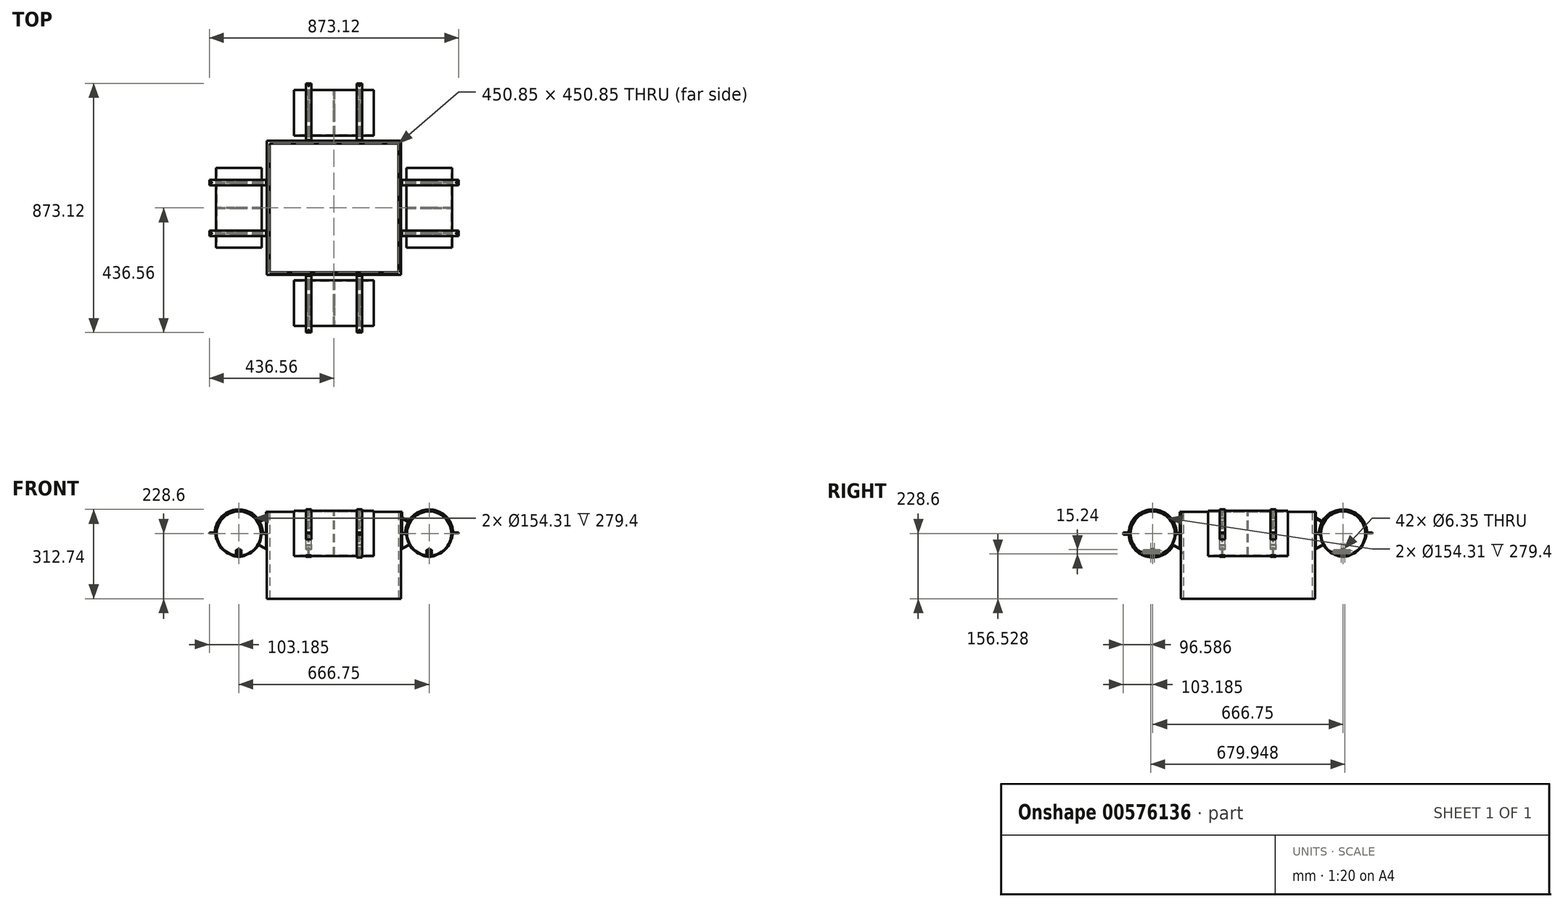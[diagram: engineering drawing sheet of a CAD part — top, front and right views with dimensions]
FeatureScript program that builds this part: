
annotation { "Feature Type Name" : "Feature", "Feature Type Description" : "" }
export const myFeature = defineFeature(function(context is Context, id is Id, definition is map)
    precondition{}
    {
        {
            var Q0;
            Q0=qCreatedBy(makeId("Front.planeOp"),FACE);
            var sketch = newSketch(context, id + "F0", { "sketchPlane" : qUnion([Q0])});
            skLineSegment(sketch, "E0", {"start": v(0, 0) * mm, "end": v(238.13, 0) * mm});
            skLineSegment(sketch, "E1", {"start": v(238.13, 0) * mm, "end": v(238.13, 228.6) * mm});
            skLineSegment(sketch, "E2", {"start": v(238.13, 228.6) * mm, "end": v(333.38, 228.6) * mm});
            skCircle(sketch, "E3", {"center": v(333.38, 228.6) * mm, "radius": 79.7 * mm});
            skCircle(sketch, "E4", {"center": v(333.38, 228.6) * mm, "radius": 77.15 * mm});
            skSolve(sketch);
        }
        {
            var Q0;
            Q0=qSketchRegion(id+"F0",true);
            extrude(context, id + "F1", {"entities" : qUnion([Q0]), "endBound" : BoundingType.SYMMETRIC, "depth" : 279.4 * mm, "offsetDistance" : 25.4 * mm});
        }
        {
            var Q0;
            Q0=qCreatedBy(makeId("Front.planeOp"),FACE);
            var sketch = newSketch(context, id + "F2", { "sketchPlane" : qUnion([Q0])});
            skLineSegment(sketch, "E5", {"start": v(0, 0) * mm, "end": v(0, 120.85) * mm});
            skSolve(sketch);
        }
        {
            var Q0;
            Q0=makeQuery(id+"F1.opExtrude","SWEPT_BODY",BODY,{"disambiguationData":[OSD([sQuery(id+"F0.wireOp",EDGE,"E3"),sQuery(id+"F0.wireOp",EDGE,"E4")])]});
            var Q1;
            Q1=sQuery(id+"F2.wireOp",EDGE,"E5");
            circularPattern(context, id + "F3", {"entities" : qUnion([Q0]), "axis" : qUnion([Q1]), "angle" : 360 * degree, "instanceCount" : 4, "equalSpace" : true});
        }
        {
            var Q0;
            Q0=qCreatedBy(makeId("Top.planeOp"),FACE);
            var sketch = newSketch(context, id + "F4", { "sketchPlane" : qUnion([Q0])});
            skLineSegment(sketch, "E6.bottom", {"start": v(234.95, -234.95) * mm, "end": v(-234.95, -234.95) * mm});
            skLineSegment(sketch, "E6.top", {"start": v(234.95, 234.95) * mm, "end": v(-234.95, 234.95) * mm});
            skLineSegment(sketch, "E6.left", {"start": v(234.95, -234.95) * mm, "end": v(234.95, 234.95) * mm});
            skLineSegment(sketch, "E6.right", {"start": v(-234.95, -234.95) * mm, "end": v(-234.95, 234.95) * mm});
            skPoint(sketch, "E6.middle", {"position": v(0, 0) * mm});
            skLineSegment(sketch, "E7.0", {"start": v(225.42, -225.42) * mm, "end": v(-225.43, -225.43) * mm});
            skLineSegment(sketch, "E7.1", {"start": v(225.42, -225.42) * mm, "end": v(225.43, 225.43) * mm});
            skLineSegment(sketch, "E7.2", {"start": v(225.43, 225.43) * mm, "end": v(-225.43, 225.43) * mm});
            skLineSegment(sketch, "E7.3", {"start": v(-225.43, -225.43) * mm, "end": v(-225.43, 225.43) * mm});
            skSolve(sketch);
        }
        {
            var Q0;
            Q0=qSketchRegion(id+"F4",true);
            extrude(context, id + "F5", {"entities" : qUnion([Q0]), "depth" : 304.8 * mm, "offsetDistance" : 25.4 * mm});
        }
        {
            var Q0;
            Q0=qCreatedBy(makeId("Right.planeOp"),FACE);
            cPlane(context, id + "F6", {"entities" : qUnion([Q0]), "cplaneType" : CPlaneType.OFFSET, "offset" : 88.9 * mm, "width" : 152.4 * mm, "height" : 152.4 * mm});
        }
        {
            var Q0;
            Q0=qCreatedBy(makeId("Right.planeOp"),FACE);
            cPlane(context, id + "F7", {"entities" : qUnion([Q0]), "cplaneType" : CPlaneType.OFFSET, "offset" : 88.9 * mm, "oppositeDirection" : true, "width" : 152.4 * mm, "height" : 152.4 * mm});
        }
        {
            var Q0;
            Q0=qCreatedBy(makeId("Right.planeOp"),FACE);
            var sketch = newSketch(context, id + "F8", { "sketchPlane" : qUnion([Q0])});
            skCircle(sketch, "E8", {"center": v(-333.38, 228.6) * mm, "radius": 77.15 * mm});
            skLineSegment(sketch, "E9", {"start": v(-333.38, 228.6) * mm, "end": v(-333.38, 151.45) * mm});
            skLineSegment(sketch, "E10", {"start": v(-333.38, 151.45) * mm, "end": v(-333.38, 156.53) * mm});
            skCircle(sketch, "E11", {"center": v(-333.38, 156.53) * mm, "radius": 3.18 * mm});
            skLineSegment(sketch, "E12", {"start": v(-333.38, 156.53) * mm, "end": v(-333.38, 164.15) * mm});
            skCircle(sketch, "E13", {"center": v(-333.38, 164.15) * mm, "radius": 3.18 * mm});
            skCircle(sketch, "E14.1.0", {"center": v(-326.78, 160.34) * mm, "radius": 3.18 * mm});
            skCircle(sketch, "E14.2.0", {"center": v(-326.78, 167.96) * mm, "radius": 3.18 * mm});
            skCircle(sketch, "E14.3.0", {"center": v(-333.38, 171.77) * mm, "radius": 3.18 * mm});
            skCircle(sketch, "E14.4.0", {"center": v(-339.97, 167.96) * mm, "radius": 3.18 * mm});
            skCircle(sketch, "E14.5.0", {"center": v(-339.97, 160.34) * mm, "radius": 3.18 * mm});
            skSolve(sketch);
        }
        {
            var Q0;
            Q0=qSketchRegion(id+"F8",true);
            extrude(context, id + "F9", {"entities" : qUnion([Q0]), "endBound" : BoundingType.SYMMETRIC, "depth" : 3.17 * mm, "offsetDistance" : 25.4 * mm});
        }
        {
            var Q0;
            Q0=qCreatedBy(id+"F6.planeOp",FACE);
            cPlane(context, id + "F10", {"entities" : qUnion([Q0]), "cplaneType" : CPlaneType.OFFSET, "offset" : 44.45 * mm, "oppositeDirection" : true, "width" : 152.4 * mm, "height" : 152.4 * mm});
        }
        {
            var Q0;
            Q0=qCreatedBy(id+"F7.planeOp",FACE);
            cPlane(context, id + "F11", {"entities" : qUnion([Q0]), "cplaneType" : CPlaneType.OFFSET, "offset" : 44.45 * mm, "width" : 152.4 * mm, "height" : 152.4 * mm});
        }
        {
            var Q0;
            Q0=makeQuery(id+"F9.opExtrude","SWEPT_BODY",BODY,{"disambiguationData":[OSD([sQuery(id+"F8.wireOp",EDGE,"E8"),sQuery(id+"F8.wireOp",EDGE,"E11"),sQuery(id+"F8.wireOp",EDGE,"E13"),sQuery(id+"F8.wireOp",EDGE,"E14.1.0"),sQuery(id+"F8.wireOp",EDGE,"E14.2.0"),sQuery(id+"F8.wireOp",EDGE,"E14.3.0"),sQuery(id+"F8.wireOp",EDGE,"E14.4.0"),sQuery(id+"F8.wireOp",EDGE,"E14.5.0")])]});
            var Q1;
            Q1=qCreatedBy(id+"F11.planeOp",FACE);
            mirror(context, id + "F12", {"entities" : qUnion([Q0]), "mirrorPlane" : qUnion([Q1])});
        }
        {
            var Q0;
            Q0=makeQuery(id+"F9.opExtrude","SWEPT_BODY",BODY,{"disambiguationData":[OSD([sQuery(id+"F8.wireOp",EDGE,"E8"),sQuery(id+"F8.wireOp",EDGE,"E11"),sQuery(id+"F8.wireOp",EDGE,"E13"),sQuery(id+"F8.wireOp",EDGE,"E14.1.0"),sQuery(id+"F8.wireOp",EDGE,"E14.2.0"),sQuery(id+"F8.wireOp",EDGE,"E14.3.0"),sQuery(id+"F8.wireOp",EDGE,"E14.4.0"),sQuery(id+"F8.wireOp",EDGE,"E14.5.0")])]});
            var Q1;
            Q1=qCreatedBy(id+"F10.planeOp",FACE);
            mirror(context, id + "F13", {"entities" : qUnion([Q0]), "mirrorPlane" : qUnion([Q1])});
        }
        {
            var Q0;
            Q0=makeQuery(id+"F13.opPattern","COPY",BODY,{"derivedFrom":makeQuery(id+"F9.opExtrude","SWEPT_BODY",BODY,{"disambiguationData":[OSD([sQuery(id+"F8.wireOp",EDGE,"E8"),sQuery(id+"F8.wireOp",EDGE,"E11"),sQuery(id+"F8.wireOp",EDGE,"E13"),sQuery(id+"F8.wireOp",EDGE,"E14.1.0"),sQuery(id+"F8.wireOp",EDGE,"E14.2.0"),sQuery(id+"F8.wireOp",EDGE,"E14.3.0"),sQuery(id+"F8.wireOp",EDGE,"E14.4.0"),sQuery(id+"F8.wireOp",EDGE,"E14.5.0")])]}),"instanceName":"1"});
            var Q1;
            Q1=makeQuery(id+"F12.opPattern","COPY",BODY,{"derivedFrom":makeQuery(id+"F9.opExtrude","SWEPT_BODY",BODY,{"disambiguationData":[OSD([sQuery(id+"F8.wireOp",EDGE,"E8"),sQuery(id+"F8.wireOp",EDGE,"E11"),sQuery(id+"F8.wireOp",EDGE,"E13"),sQuery(id+"F8.wireOp",EDGE,"E14.1.0"),sQuery(id+"F8.wireOp",EDGE,"E14.2.0"),sQuery(id+"F8.wireOp",EDGE,"E14.3.0"),sQuery(id+"F8.wireOp",EDGE,"E14.4.0"),sQuery(id+"F8.wireOp",EDGE,"E14.5.0")])]}),"instanceName":"1"});
            var Q2;
            Q2=makeQuery(id+"F9.opExtrude","SWEPT_BODY",BODY,{"disambiguationData":[OSD([sQuery(id+"F8.wireOp",EDGE,"E8"),sQuery(id+"F8.wireOp",EDGE,"E11"),sQuery(id+"F8.wireOp",EDGE,"E13"),sQuery(id+"F8.wireOp",EDGE,"E14.1.0"),sQuery(id+"F8.wireOp",EDGE,"E14.2.0"),sQuery(id+"F8.wireOp",EDGE,"E14.3.0"),sQuery(id+"F8.wireOp",EDGE,"E14.4.0"),sQuery(id+"F8.wireOp",EDGE,"E14.5.0")])]});
            var Q3;
            Q3=sQuery(id+"F2.wireOp",EDGE,"E5");
            circularPattern(context, id + "F14", {"entities" : qUnion([Q0, Q1, Q2]), "axis" : qUnion([Q3]), "angle" : 360 * degree, "instanceCount" : 4, "equalSpace" : true});
        }
        {
            var Q0;
            Q0=qCreatedBy(id+"F6.planeOp",FACE);
            var sketch = newSketch(context, id + "F15", { "sketchPlane" : qUnion([Q0])});
            skCircle(sketch, "E15", {"center": v(-333.38, 228.6) * mm, "radius": 81.28 * mm});
            skCircle(sketch, "E16", {"center": v(-333.38, 228.6) * mm, "radius": 79.7 * mm});
            skLineSegment(sketch, "E17", {"start": v(-333.38, 228.6) * mm, "end": v(-333.38, 309.88) * mm});
            skLineSegment(sketch, "E18", {"start": v(-333.38, 228.6) * mm, "end": v(-312.34, 307.11) * mm});
            skLineSegment(sketch, "E19.MirrorCS", {"start": v(-333.38, 228.6) * mm, "end": v(-354.41, 307.11) * mm});
            skLineSegment(sketch, "E20.1.0", {"start": v(-333.38, 228.6) * mm, "end": v(-411.89, 249.64) * mm});
            skLineSegment(sketch, "E20.1.1", {"start": v(-333.38, 228.6) * mm, "end": v(-411.89, 207.56) * mm});
            skLineSegment(sketch, "E20.2.0", {"start": v(-333.38, 228.6) * mm, "end": v(-354.41, 150.09) * mm});
            skLineSegment(sketch, "E20.2.1", {"start": v(-333.38, 228.6) * mm, "end": v(-312.34, 150.09) * mm});
            skLineSegment(sketch, "E20.3.0", {"start": v(-333.38, 228.6) * mm, "end": v(-254.86, 207.56) * mm});
            skLineSegment(sketch, "E20.3.1", {"start": v(-333.38, 228.6) * mm, "end": v(-254.86, 249.64) * mm});
            skLineSegment(sketch, "E21", {"start": v(-414.66, 228.6) * mm, "end": v(-417.51, 228.6) * mm});
            skLineSegment(sketch, "E22", {"start": v(-417.51, 228.6) * mm, "end": v(-436.56, 228.6) * mm});
            skLineSegment(sketch, "E23", {"start": v(-436.56, 229.1) * mm, "end": v(-436.56, 232.28) * mm});
            skLineSegment(sketch, "E24", {"start": v(-436.56, 232.28) * mm, "end": v(-419.83, 232.28) * mm});
            skLineSegment(sketch, "E25", {"start": v(-436.56, 229.1) * mm, "end": v(-417.51, 229.1) * mm});
            skLineSegment(sketch, "E26", {"start": v(-417.51, 229.1) * mm, "end": v(-414.65, 229.1) * mm});
            skPoint(sketch, "E27.visualSharp", {"position": v(-417.43, 232.28) * mm});
            skArc(sketch, "E27.filletArc", {"start": v(-419.83, 232.28) * mm, "mid": v(-418.1, 232.96) * mm, "end": v(-417.3, 234.64) * mm});
            skLineSegment(sketch, "E28.MirrorCS", {"start": v(-436.56, 228.1) * mm, "end": v(-417.51, 228.1) * mm});
            skPoint(sketch, "E29.MirrorP", {"position": v(-417.43, 224.92) * mm});
            skArc(sketch, "E30.MirrorCS", {"start": v(-419.83, 224.92) * mm, "mid": v(-418.1, 224.24) * mm, "end": v(-417.3, 222.56) * mm});
            skLineSegment(sketch, "E31.MirrorCS", {"start": v(-436.56, 224.92) * mm, "end": v(-419.83, 224.92) * mm});
            skLineSegment(sketch, "E32.MirrorCS", {"start": v(-436.56, 228.1) * mm, "end": v(-436.56, 224.92) * mm});
            skArc(sketch, "E33.trimOffspring", {"start": v(-417.3, 222.56) * mm, "mid": v(-330.35, 144.52) * mm, "end": v(-249.24, 228.6) * mm});
            skPoint(sketch, "E34.MirrorCS.start.orphan", {"position": v(-436.56, 228.6) * mm});
            skLineSegment(sketch, "E35", {"start": v(-417.51, 228.1) * mm, "end": v(-414.65, 228.1) * mm});
            skLineSegment(sketch, "E36", {"start": v(-333.38, 228.6) * mm, "end": v(-249.24, 228.6) * mm});
            skLineSegment(sketch, "E37", {"start": v(-249.24, 228.6) * mm, "end": v(-234.95, 228.6) * mm});
            skLineSegment(sketch, "E38", {"start": v(-333.38, 228.6) * mm, "end": v(-260.5, 270.67) * mm});
            skLineSegment(sketch, "E39", {"start": v(-260.5, 270.67) * mm, "end": v(-234.95, 285.43) * mm});
            skLineSegment(sketch, "E40", {"start": v(-234.95, 285.43) * mm, "end": v(-234.95, 304.48) * mm});
            skLineSegment(sketch, "E41", {"start": v(-234.95, 304.48) * mm, "end": v(-238.12, 304.48) * mm});
            skLineSegment(sketch, "E42", {"start": v(-238.13, 304.48) * mm, "end": v(-238.13, 286.9) * mm});
            skLineSegment(sketch, "E43", {"start": v(-234.95, 228.6) * mm, "end": v(-234.95, 230.19) * mm});
            skLineSegment(sketch, "E44", {"start": v(-240.67, 230.19) * mm, "end": v(-246.8, 230.19) * mm});
            skLineSegment(sketch, "E45", {"start": v(-234.95, 304.48) * mm, "end": v(-234.95, 228.6) * mm});
            skArc(sketch, "E46.trimOffspring", {"start": v(-249.33, 232.6) * mm, "mid": v(-252.1, 250.38) * mm, "end": v(-258.59, 267.15) * mm});
            skLineSegment(sketch, "E47", {"start": v(-234.95, 285.43) * mm, "end": v(-235.74, 286.8) * mm});
            skLineSegment(sketch, "E48", {"start": v(-234.95, 285.43) * mm, "end": v(-234.16, 284.05) * mm});
            skLineSegment(sketch, "E49", {"start": v(-234.16, 284.05) * mm, "end": v(-234.95, 283.6) * mm});
            skLineSegment(sketch, "E50", {"start": v(-239.4, 284.7) * mm, "end": v(-259.19, 273.26) * mm});
            skArc(sketch, "E51.trimOffspring", {"start": v(-262.6, 274.1) * mm, "mid": v(-354.17, 310.13) * mm, "end": v(-417.3, 234.64) * mm});
            skLineSegment(sketch, "E52.trimOffspring", {"start": v(-238.13, 277.36) * mm, "end": v(-238.13, 232.73) * mm});
            skLineSegment(sketch, "E53.trimOffspring", {"start": v(-241.94, 279.56) * mm, "end": v(-257.6, 270.51) * mm});
            skPoint(sketch, "E54.visualSharp", {"position": v(-238.13, 285.43) * mm});
            skArc(sketch, "E54.filletArc", {"start": v(-239.4, 284.7) * mm, "mid": v(-238.47, 285.62) * mm, "end": v(-238.12, 286.9) * mm});
            skPoint(sketch, "E55.visualSharp", {"position": v(-261.32, 272.04) * mm});
            skArc(sketch, "E55.filletArc", {"start": v(-262.6, 274.1) * mm, "mid": v(-261.06, 273) * mm, "end": v(-259.19, 273.26) * mm});
            skPoint(sketch, "E56.visualSharp", {"position": v(-259.73, 269.29) * mm});
            skArc(sketch, "E56.filletArc", {"start": v(-257.6, 270.51) * mm, "mid": v(-258.77, 269.03) * mm, "end": v(-258.59, 267.15) * mm});
            skPoint(sketch, "E57.visualSharp", {"position": v(-238.13, 281.76) * mm});
            skArc(sketch, "E57.filletArc", {"start": v(-238.13, 277.36) * mm, "mid": v(-239.4, 279.56) * mm, "end": v(-241.94, 279.56) * mm});
            skPoint(sketch, "E58.visualSharp", {"position": v(-249.25, 230.19) * mm});
            skArc(sketch, "E58.filletArc", {"start": v(-249.33, 232.6) * mm, "mid": v(-248.55, 230.89) * mm, "end": v(-246.8, 230.19) * mm});
            skPoint(sketch, "E59.visualSharp", {"position": v(-238.13, 230.19) * mm});
            skArc(sketch, "E59.filletArc", {"start": v(-240.67, 230.19) * mm, "mid": v(-238.87, 230.93) * mm, "end": v(-238.13, 232.73) * mm});
            skLineSegment(sketch, "E60.MirrorCS", {"start": v(-234.95, 171.77) * mm, "end": v(-235.74, 170.4) * mm});
            skLineSegment(sketch, "E61.MirrorCS", {"start": v(-234.95, 171.77) * mm, "end": v(-234.16, 173.15) * mm});
            skLineSegment(sketch, "E62.MirrorCS", {"start": v(-234.16, 173.15) * mm, "end": v(-234.95, 173.6) * mm});
            skArc(sketch, "E63.MirrorCS", {"start": v(-239.4, 172.5) * mm, "mid": v(-238.47, 171.58) * mm, "end": v(-238.12, 170.3) * mm});
            skLineSegment(sketch, "E64.MirrorCS", {"start": v(-234.95, 228.6) * mm, "end": v(-234.95, 227.01) * mm});
            skArc(sketch, "E65.MirrorCS", {"start": v(-262.6, 183.1) * mm, "mid": v(-261.06, 184.2) * mm, "end": v(-259.19, 183.94) * mm});
            skArc(sketch, "E66.MirrorCS", {"start": v(-240.67, 227.01) * mm, "mid": v(-238.87, 226.27) * mm, "end": v(-238.13, 224.47) * mm});
            skLineSegment(sketch, "E67.MirrorCS", {"start": v(-234.95, 152.72) * mm, "end": v(-238.12, 152.72) * mm});
            skArc(sketch, "E68.MirrorCS", {"start": v(-257.6, 186.69) * mm, "mid": v(-258.77, 188.17) * mm, "end": v(-258.59, 190.05) * mm});
            skArc(sketch, "E69.MirrorCS", {"start": v(-249.33, 224.6) * mm, "mid": v(-248.55, 226.31) * mm, "end": v(-246.8, 227.01) * mm});
            skArc(sketch, "E70.MirrorCS", {"start": v(-238.13, 179.84) * mm, "mid": v(-239.4, 177.64) * mm, "end": v(-241.94, 177.64) * mm});
            skLineSegment(sketch, "E71.MirrorCS", {"start": v(-234.95, 171.77) * mm, "end": v(-234.95, 152.72) * mm});
            skLineSegment(sketch, "E72.MirrorCS", {"start": v(-333.38, 228.6) * mm, "end": v(-260.5, 186.53) * mm});
            skPoint(sketch, "E73.MirrorP", {"position": v(-259.73, 187.91) * mm});
            skLineSegment(sketch, "E74.MirrorCS", {"start": v(-260.5, 186.53) * mm, "end": v(-234.95, 171.77) * mm});
            skLineSegment(sketch, "E75.MirrorCS", {"start": v(-240.67, 227.01) * mm, "end": v(-246.8, 227.01) * mm});
            skLineSegment(sketch, "E76.MirrorCS", {"start": v(-239.4, 172.5) * mm, "end": v(-259.19, 183.94) * mm});
            skPoint(sketch, "E77.MirrorP", {"position": v(-238.13, 175.44) * mm});
            skPoint(sketch, "E78.MirrorP", {"position": v(-261.32, 185.16) * mm});
            skArc(sketch, "E79.MirrorCS", {"start": v(-249.33, 224.6) * mm, "mid": v(-252.1, 206.82) * mm, "end": v(-258.59, 190.05) * mm});
            skLineSegment(sketch, "E80.MirrorCS", {"start": v(-238.13, 179.84) * mm, "end": v(-238.13, 224.47) * mm});
            skPoint(sketch, "E81.MirrorP", {"position": v(-238.13, 227.01) * mm});
            skPoint(sketch, "E82.MirrorP", {"position": v(-249.25, 227.01) * mm});
            skPoint(sketch, "E83.MirrorP", {"position": v(-238.13, 171.77) * mm});
            skLineSegment(sketch, "E84.MirrorCS", {"start": v(-241.94, 177.64) * mm, "end": v(-257.6, 186.69) * mm});
            skLineSegment(sketch, "E85.MirrorCS", {"start": v(-234.95, 152.72) * mm, "end": v(-234.95, 228.6) * mm});
            skLineSegment(sketch, "E86.MirrorCS", {"start": v(-238.13, 152.72) * mm, "end": v(-238.13, 170.3) * mm});
            skSolve(sketch);
        }
        {
            var Q0;
            {var subQ0=sQuery(id+"F15.wireOp",EDGE,"E48");Q0=makeQuery(id+"F15.imprint","IMPRINT",FACE,{"disambiguationData":[TD([[makeQuery(id+"F15.imprint","IMPRINT",EDGE,{"derivedFrom":subQ0}),-1.0]])]});}
            var Q1;
            {var subQ0=sQuery(id+"F15.wireOp",EDGE,"E61.MirrorCS");Q1=makeQuery(id+"F15.imprint","IMPRINT",FACE,{"disambiguationData":[TD([[makeQuery(id+"F15.imprint","IMPRINT",EDGE,{"derivedFrom":subQ0}),1.0]])]});}
            var Q2;
            Q2=makeQuery(id+"F15.imprint","IMPRINT",FACE,{"disambiguationData":[TD([[makeQuery(id+"F15.imprint","IMPRINT",EDGE,{"derivedFrom":sQuery(id+"F15.wireOp",EDGE,"E63.MirrorCS")}),1.0]])]});
            var Q3;
            {var subQ5=sQuery(id+"F15.wireOp",EDGE,"E37");Q3=makeQuery(id+"F15.imprint","IMPRINT",FACE,{"disambiguationData":[TD([[makeQuery(id+"F15.imprint","IMPRINT",EDGE,{"derivedFrom":subQ5}),-1.0]])]});}
            var Q4;
            Q4=makeQuery(id+"F15.imprint","IMPRINT",FACE,{"disambiguationData":[TD([[makeQuery(id+"F15.imprint","IMPRINT",EDGE,{"derivedFrom":sQuery(id+"F15.wireOp",EDGE,"E23")}),-1.0]])]});
            var Q5;
            Q5=makeQuery(id+"F15.imprint","IMPRINT",FACE,{"disambiguationData":[TD([[makeQuery(id+"F15.imprint","IMPRINT",EDGE,{"derivedFrom":sQuery(id+"F15.wireOp",EDGE,"E28.MirrorCS")}),-1.0]])]});
            var Q6;
            {var subQ1=sQuery(id+"F15.wireOp",EDGE,"E37");Q6=makeQuery(id+"F15.imprint","IMPRINT",FACE,{"disambiguationData":[TD([[makeQuery(id+"F15.imprint","IMPRINT",EDGE,{"derivedFrom":subQ1}),1.0]])]});}
            var Q7;
            {var subQ0=sQuery(id+"F15.wireOp",EDGE,"E79.MirrorCS");Q7=makeQuery(id+"F15.imprint","IMPRINT",FACE,{"disambiguationData":[TD([[makeQuery(id+"F15.imprint","IMPRINT",EDGE,{"derivedFrom":subQ0}),-1.0]])]});}
            extrude(context, id + "F16", {"entities" : qUnion([Q0, Q1, Q2, Q3, Q4, Q5, Q6, Q7]), "endBound" : BoundingType.SYMMETRIC, "depth" : 19.05 * mm, "offsetDistance" : 25.4 * mm});
        }
        {
            var Q0;
            {var subQ1=sQuery(id+"F15.wireOp",EDGE,"E15");var subQ4=makeQuery(id+"F15.imprint","IMPRINT",VERTEX,{"derivedFrom":subQ1});Q0=makeQuery(id+"F15.imprint","IMPRINT",FACE,{"disambiguationData":[TD([[makeQuery(id+"F15.imprint","IMPRINT",EDGE,{"disambiguationData":[TD([[subQ4,1.0]])],"derivedFrom":subQ1}),1.0]])]});}
            var Q1;
            {var subQ0=sQuery(id+"F15.wireOp",EDGE,"E17");var subQ1=sQuery(id+"F15.wireOp",EDGE,"E15");var subQ2=makeQuery(id+"F15.imprint","INTERSECT",VERTEX,{"derivedFrom":[subQ1,subQ0]});Q1=makeQuery(id+"F15.imprint","IMPRINT",FACE,{"disambiguationData":[TD([[makeQuery(id+"F15.imprint","IMPRINT",EDGE,{"disambiguationData":[TD([[subQ2,-1.0]])],"derivedFrom":subQ1}),1.0]])]});}
            var Q2;
            {var subQ0=sQuery(id+"F15.wireOp",EDGE,"E17");var subQ1=sQuery(id+"F15.wireOp",EDGE,"E15");var subQ2=makeQuery(id+"F15.imprint","INTERSECT",VERTEX,{"derivedFrom":[subQ1,subQ0]});Q2=makeQuery(id+"F15.imprint","IMPRINT",FACE,{"disambiguationData":[TD([[makeQuery(id+"F15.imprint","IMPRINT",EDGE,{"disambiguationData":[TD([[subQ2,1.0]])],"derivedFrom":subQ1}),1.0]])]});}
            var Q3;
            {var subQ0=sQuery(id+"F15.wireOp",EDGE,"E20.3.1");var subQ1=sQuery(id+"F15.wireOp",EDGE,"E15");var subQ2=makeQuery(id+"F15.imprint","INTERSECT",VERTEX,{"derivedFrom":[subQ1,subQ0]});Q3=makeQuery(id+"F15.imprint","IMPRINT",FACE,{"disambiguationData":[TD([[makeQuery(id+"F15.imprint","IMPRINT",EDGE,{"disambiguationData":[TD([[subQ2,1.0]])],"derivedFrom":subQ1}),1.0]])]});}
            var Q4;
            {var subQ0=sQuery(id+"F15.wireOp",EDGE,"E20.3.0");var subQ1=sQuery(id+"F15.wireOp",EDGE,"E15");var subQ2=makeQuery(id+"F15.imprint","INTERSECT",VERTEX,{"derivedFrom":[subQ1,subQ0]});Q4=makeQuery(id+"F15.imprint","IMPRINT",FACE,{"disambiguationData":[TD([[makeQuery(id+"F15.imprint","IMPRINT",EDGE,{"disambiguationData":[TD([[subQ2,-1.0]])],"derivedFrom":subQ1}),1.0]])]});}
            var Q5;
            {var subQ0=sQuery(id+"F15.wireOp",EDGE,"E20.2.0");var subQ1=sQuery(id+"F15.wireOp",EDGE,"E15");var subQ2=makeQuery(id+"F15.imprint","INTERSECT",VERTEX,{"derivedFrom":[subQ1,subQ0]});Q5=makeQuery(id+"F15.imprint","IMPRINT",FACE,{"disambiguationData":[TD([[makeQuery(id+"F15.imprint","IMPRINT",EDGE,{"disambiguationData":[TD([[subQ2,-1.0]])],"derivedFrom":subQ1}),1.0]])]});}
            extrude(context, id + "F17", {"entities" : qUnion([Q0, Q1, Q2, Q3, Q4, Q5]), "endBound" : BoundingType.SYMMETRIC, "depth" : 19.05 * mm, "offsetDistance" : 25.4 * mm});
        }
        {
            var Q0;
            Q0=makeQuery(id+"F16.opExtrude","SWEPT_FACE",FACE,{"disambiguationData":[OSD([sQuery(id+"F15.wireOp",EDGE,"E24")])]});
            var sketch = newSketch(context, id + "F18", { "sketchPlane" : qUnion([Q0])});
            skLineSegment(sketch, "E87", {"start": v(88.9, -436.56) * mm, "end": v(88.9, -428.94) * mm});
            skSolve(sketch);
        }
        {
            var Q0;
            Q0=sQuery(id+"F18.wireOp",VERTEX,"E87.end");
            var Q1;
            Q1=makeQuery(id+"F16.opExtrude","SWEPT_BODY",BODY,{"disambiguationData":[OSD([sQuery(id+"F15.wireOp",EDGE,"E15"),sQuery(id+"F15.wireOp",EDGE,"E23"),sQuery(id+"F15.wireOp",EDGE,"E24"),sQuery(id+"F15.wireOp",EDGE,"E25"),sQuery(id+"F15.wireOp",EDGE,"E26"),sQuery(id+"F15.wireOp",EDGE,"E27.filletArc"),sQuery(id+"F15.wireOp",EDGE,"E28.MirrorCS"),sQuery(id+"F15.wireOp",EDGE,"E30.MirrorCS"),sQuery(id+"F15.wireOp",EDGE,"E31.MirrorCS"),sQuery(id+"F15.wireOp",EDGE,"E32.MirrorCS"),sQuery(id+"F15.wireOp",EDGE,"E33.trimOffspring"),sQuery(id+"F15.wireOp",EDGE,"E35"),sQuery(id+"F15.wireOp",EDGE,"E41"),sQuery(id+"F15.wireOp",EDGE,"E42"),sQuery(id+"F15.wireOp",EDGE,"E44"),sQuery(id+"F15.wireOp",EDGE,"E45"),sQuery(id+"F15.wireOp",EDGE,"E46.trimOffspring"),sQuery(id+"F15.wireOp",EDGE,"E48"),sQuery(id+"F15.wireOp",EDGE,"E49"),sQuery(id+"F15.wireOp",EDGE,"E50"),sQuery(id+"F15.wireOp",EDGE,"E51.trimOffspring"),sQuery(id+"F15.wireOp",EDGE,"E52.trimOffspring"),sQuery(id+"F15.wireOp",EDGE,"E53.trimOffspring"),sQuery(id+"F15.wireOp",EDGE,"E54.filletArc"),sQuery(id+"F15.wireOp",EDGE,"E55.filletArc"),sQuery(id+"F15.wireOp",EDGE,"E56.filletArc"),sQuery(id+"F15.wireOp",EDGE,"E57.filletArc"),sQuery(id+"F15.wireOp",EDGE,"E58.filletArc"),sQuery(id+"F15.wireOp",EDGE,"E59.filletArc"),sQuery(id+"F15.wireOp",EDGE,"E61.MirrorCS"),sQuery(id+"F15.wireOp",EDGE,"E62.MirrorCS"),sQuery(id+"F15.wireOp",EDGE,"E63.MirrorCS"),sQuery(id+"F15.wireOp",EDGE,"E65.MirrorCS"),sQuery(id+"F15.wireOp",EDGE,"E66.MirrorCS"),sQuery(id+"F15.wireOp",EDGE,"E67.MirrorCS"),sQuery(id+"F15.wireOp",EDGE,"E68.MirrorCS"),sQuery(id+"F15.wireOp",EDGE,"E69.MirrorCS"),sQuery(id+"F15.wireOp",EDGE,"E70.MirrorCS"),sQuery(id+"F15.wireOp",EDGE,"E75.MirrorCS"),sQuery(id+"F15.wireOp",EDGE,"E76.MirrorCS"),sQuery(id+"F15.wireOp",EDGE,"E79.MirrorCS"),sQuery(id+"F15.wireOp",EDGE,"E80.MirrorCS"),sQuery(id+"F15.wireOp",EDGE,"E84.MirrorCS"),sQuery(id+"F15.wireOp",EDGE,"E85.MirrorCS"),sQuery(id+"F15.wireOp",EDGE,"E86.MirrorCS")])]});
            hole(context, id + "F19", {"style" : HoleStyle.SIMPLE, "endStyle" : HoleEndStyle.BLIND, "standardTappedOrClearance" : lookupTablePath({ "standard" : "ANSI", "fit" : "Close", "size" : "#8", "type" : "Clearance" }), "standardBlindInLast" : lookupTablePath({ "fit" : "Close", "standard" : "ANSI", "size" : "#8", "type" : "Clearance" }), "holeDiameter" : 4.32 * mm, "holeDepth" : 12.7 * mm, "isTappedThrough" : true, "tappedDepth" : 10.8 * mm, "tapClearance" : 3, "locations" : qUnion([Q0]), "scope" : qUnion([Q1])});
        }
        {
            var Q0;
            Q0=makeQuery(id+"F16.opExtrude","SWEPT_FACE",FACE,{"disambiguationData":[OSD([sQuery(id+"F15.wireOp",EDGE,"E42")])]});
            var sketch = newSketch(context, id + "F20", { "sketchPlane" : qUnion([Q0])});
            skLineSegment(sketch, "E88", {"start": v(88.9, 304.48) * mm, "end": v(88.9, 296.86) * mm});
            skLineSegment(sketch, "E89", {"start": v(98.42, 304.48) * mm, "end": v(98.43, 152.72) * mm});
            skLineSegment(sketch, "E90", {"start": v(98.42, 228.6) * mm, "end": v(119.41, 228.6) * mm});
            skPoint(sketch, "E90.endSnap0", {"position": v(98.42, 228.6) * mm});
            skLineSegment(sketch, "E91.MirrorCS", {"start": v(88.9, 152.72) * mm, "end": v(88.9, 160.34) * mm});
            skSolve(sketch);
        }
        {
            var Q0;
            Q0=sQuery(id+"F20.wireOp",VERTEX,"E88.end");
            var Q1;
            Q1=sQuery(id+"F20.wireOp",VERTEX,"E91.MirrorCS.end");
            var Q2;
            Q2=makeQuery(id+"F16.opExtrude","SWEPT_BODY",BODY,{"disambiguationData":[OSD([sQuery(id+"F15.wireOp",EDGE,"E15"),sQuery(id+"F15.wireOp",EDGE,"E23"),sQuery(id+"F15.wireOp",EDGE,"E24"),sQuery(id+"F15.wireOp",EDGE,"E25"),sQuery(id+"F15.wireOp",EDGE,"E26"),sQuery(id+"F15.wireOp",EDGE,"E27.filletArc"),sQuery(id+"F15.wireOp",EDGE,"E28.MirrorCS"),sQuery(id+"F15.wireOp",EDGE,"E30.MirrorCS"),sQuery(id+"F15.wireOp",EDGE,"E31.MirrorCS"),sQuery(id+"F15.wireOp",EDGE,"E32.MirrorCS"),sQuery(id+"F15.wireOp",EDGE,"E33.trimOffspring"),sQuery(id+"F15.wireOp",EDGE,"E35"),sQuery(id+"F15.wireOp",EDGE,"E41"),sQuery(id+"F15.wireOp",EDGE,"E42"),sQuery(id+"F15.wireOp",EDGE,"E44"),sQuery(id+"F15.wireOp",EDGE,"E45"),sQuery(id+"F15.wireOp",EDGE,"E46.trimOffspring"),sQuery(id+"F15.wireOp",EDGE,"E48"),sQuery(id+"F15.wireOp",EDGE,"E49"),sQuery(id+"F15.wireOp",EDGE,"E50"),sQuery(id+"F15.wireOp",EDGE,"E51.trimOffspring"),sQuery(id+"F15.wireOp",EDGE,"E52.trimOffspring"),sQuery(id+"F15.wireOp",EDGE,"E53.trimOffspring"),sQuery(id+"F15.wireOp",EDGE,"E54.filletArc"),sQuery(id+"F15.wireOp",EDGE,"E55.filletArc"),sQuery(id+"F15.wireOp",EDGE,"E56.filletArc"),sQuery(id+"F15.wireOp",EDGE,"E57.filletArc"),sQuery(id+"F15.wireOp",EDGE,"E58.filletArc"),sQuery(id+"F15.wireOp",EDGE,"E59.filletArc"),sQuery(id+"F15.wireOp",EDGE,"E61.MirrorCS"),sQuery(id+"F15.wireOp",EDGE,"E62.MirrorCS"),sQuery(id+"F15.wireOp",EDGE,"E63.MirrorCS"),sQuery(id+"F15.wireOp",EDGE,"E65.MirrorCS"),sQuery(id+"F15.wireOp",EDGE,"E66.MirrorCS"),sQuery(id+"F15.wireOp",EDGE,"E67.MirrorCS"),sQuery(id+"F15.wireOp",EDGE,"E68.MirrorCS"),sQuery(id+"F15.wireOp",EDGE,"E69.MirrorCS"),sQuery(id+"F15.wireOp",EDGE,"E70.MirrorCS"),sQuery(id+"F15.wireOp",EDGE,"E75.MirrorCS"),sQuery(id+"F15.wireOp",EDGE,"E76.MirrorCS"),sQuery(id+"F15.wireOp",EDGE,"E79.MirrorCS"),sQuery(id+"F15.wireOp",EDGE,"E80.MirrorCS"),sQuery(id+"F15.wireOp",EDGE,"E84.MirrorCS"),sQuery(id+"F15.wireOp",EDGE,"E85.MirrorCS"),sQuery(id+"F15.wireOp",EDGE,"E86.MirrorCS")])]});
            var Q3;
            Q3=makeQuery(id+"F5.opExtrude","SWEPT_BODY",BODY,{"disambiguationData":[OSD([sQuery(id+"F4.wireOp",EDGE,"E6.bottom"),sQuery(id+"F4.wireOp",EDGE,"E6.top"),sQuery(id+"F4.wireOp",EDGE,"E6.left"),sQuery(id+"F4.wireOp",EDGE,"E6.right"),sQuery(id+"F4.wireOp",EDGE,"E7.0"),sQuery(id+"F4.wireOp",EDGE,"E7.1"),sQuery(id+"F4.wireOp",EDGE,"E7.2"),sQuery(id+"F4.wireOp",EDGE,"E7.3")])]});
            hole(context, id + "F21", {"style" : HoleStyle.SIMPLE, "endStyle" : HoleEndStyle.BLIND, "standardTappedOrClearance" : lookupTablePath({ "standard" : "ANSI", "fit" : "Close", "size" : "#8", "type" : "Clearance" }), "standardBlindInLast" : lookupTablePath({ "fit" : "Close", "standard" : "ANSI", "size" : "#8", "type" : "Clearance" }), "holeDiameter" : 4.32 * mm, "holeDepth" : 12.7 * mm, "isTappedThrough" : true, "tappedDepth" : 10.8 * mm, "tapClearance" : 3, "locations" : qUnion([Q0, Q1]), "scope" : qUnion([Q2, Q3])});
        }
        {
            var Q0;
            Q0=makeQuery(id+"F17.opExtrude","SWEPT_BODY",BODY,{"disambiguationData":[OSD([sQuery(id+"F15.wireOp",EDGE,"E15"),sQuery(id+"F15.wireOp",EDGE,"E16"),sQuery(id+"F15.wireOp",EDGE,"E20.2.0"),sQuery(id+"F15.wireOp",EDGE,"E20.2.1")])]});
            var Q1;
            Q1=makeQuery(id+"F17.opExtrude","SWEPT_BODY",BODY,{"disambiguationData":[OSD([sQuery(id+"F15.wireOp",EDGE,"E15"),sQuery(id+"F15.wireOp",EDGE,"E16"),sQuery(id+"F15.wireOp",EDGE,"E20.1.0"),sQuery(id+"F15.wireOp",EDGE,"E20.1.1")])]});
            var Q2;
            Q2=makeQuery(id+"F17.opExtrude","SWEPT_BODY",BODY,{"disambiguationData":[OSD([sQuery(id+"F15.wireOp",EDGE,"E15"),sQuery(id+"F15.wireOp",EDGE,"E16"),sQuery(id+"F15.wireOp",EDGE,"E18"),sQuery(id+"F15.wireOp",EDGE,"E19.MirrorCS")])]});
            var Q3;
            Q3=makeQuery(id+"F17.opExtrude","SWEPT_BODY",BODY,{"disambiguationData":[OSD([sQuery(id+"F15.wireOp",EDGE,"E15"),sQuery(id+"F15.wireOp",EDGE,"E16"),sQuery(id+"F15.wireOp",EDGE,"E20.3.1"),sQuery(id+"F15.wireOp",EDGE,"E20.3.0")])]});
            var Q4;
            Q4=makeQuery(id+"F16.opExtrude","SWEPT_BODY",BODY,{"disambiguationData":[OSD([sQuery(id+"F15.wireOp",EDGE,"E15"),sQuery(id+"F15.wireOp",EDGE,"E23"),sQuery(id+"F15.wireOp",EDGE,"E24"),sQuery(id+"F15.wireOp",EDGE,"E25"),sQuery(id+"F15.wireOp",EDGE,"E26"),sQuery(id+"F15.wireOp",EDGE,"E27.filletArc"),sQuery(id+"F15.wireOp",EDGE,"E28.MirrorCS"),sQuery(id+"F15.wireOp",EDGE,"E30.MirrorCS"),sQuery(id+"F15.wireOp",EDGE,"E31.MirrorCS"),sQuery(id+"F15.wireOp",EDGE,"E32.MirrorCS"),sQuery(id+"F15.wireOp",EDGE,"E33.trimOffspring"),sQuery(id+"F15.wireOp",EDGE,"E35"),sQuery(id+"F15.wireOp",EDGE,"E41"),sQuery(id+"F15.wireOp",EDGE,"E42"),sQuery(id+"F15.wireOp",EDGE,"E44"),sQuery(id+"F15.wireOp",EDGE,"E45"),sQuery(id+"F15.wireOp",EDGE,"E46.trimOffspring"),sQuery(id+"F15.wireOp",EDGE,"E48"),sQuery(id+"F15.wireOp",EDGE,"E49"),sQuery(id+"F15.wireOp",EDGE,"E50"),sQuery(id+"F15.wireOp",EDGE,"E51.trimOffspring"),sQuery(id+"F15.wireOp",EDGE,"E52.trimOffspring"),sQuery(id+"F15.wireOp",EDGE,"E53.trimOffspring"),sQuery(id+"F15.wireOp",EDGE,"E54.filletArc"),sQuery(id+"F15.wireOp",EDGE,"E55.filletArc"),sQuery(id+"F15.wireOp",EDGE,"E56.filletArc"),sQuery(id+"F15.wireOp",EDGE,"E57.filletArc"),sQuery(id+"F15.wireOp",EDGE,"E58.filletArc"),sQuery(id+"F15.wireOp",EDGE,"E59.filletArc"),sQuery(id+"F15.wireOp",EDGE,"E61.MirrorCS"),sQuery(id+"F15.wireOp",EDGE,"E62.MirrorCS"),sQuery(id+"F15.wireOp",EDGE,"E63.MirrorCS"),sQuery(id+"F15.wireOp",EDGE,"E65.MirrorCS"),sQuery(id+"F15.wireOp",EDGE,"E66.MirrorCS"),sQuery(id+"F15.wireOp",EDGE,"E67.MirrorCS"),sQuery(id+"F15.wireOp",EDGE,"E68.MirrorCS"),sQuery(id+"F15.wireOp",EDGE,"E69.MirrorCS"),sQuery(id+"F15.wireOp",EDGE,"E70.MirrorCS"),sQuery(id+"F15.wireOp",EDGE,"E75.MirrorCS"),sQuery(id+"F15.wireOp",EDGE,"E76.MirrorCS"),sQuery(id+"F15.wireOp",EDGE,"E79.MirrorCS"),sQuery(id+"F15.wireOp",EDGE,"E80.MirrorCS"),sQuery(id+"F15.wireOp",EDGE,"E84.MirrorCS"),sQuery(id+"F15.wireOp",EDGE,"E85.MirrorCS"),sQuery(id+"F15.wireOp",EDGE,"E86.MirrorCS")])]});
            var Q5;
            Q5=qCreatedBy(makeId("Right.planeOp"),FACE);
            mirror(context, id + "F22", {"entities" : qUnion([Q0, Q1, Q2, Q3, Q4]), "mirrorPlane" : qUnion([Q5])});
        }
        {
            var Q0;
            Q0=makeQuery(id+"F22.opPattern","COPY",BODY,{"derivedFrom":makeQuery(id+"F17.opExtrude","SWEPT_BODY",BODY,{"disambiguationData":[OSD([sQuery(id+"F15.wireOp",EDGE,"E15"),sQuery(id+"F15.wireOp",EDGE,"E16"),sQuery(id+"F15.wireOp",EDGE,"E20.2.0"),sQuery(id+"F15.wireOp",EDGE,"E20.2.1")])]}),"instanceName":"1"});
            var Q1;
            Q1=makeQuery(id+"F22.opPattern","COPY",BODY,{"derivedFrom":makeQuery(id+"F17.opExtrude","SWEPT_BODY",BODY,{"disambiguationData":[OSD([sQuery(id+"F15.wireOp",EDGE,"E15"),sQuery(id+"F15.wireOp",EDGE,"E16"),sQuery(id+"F15.wireOp",EDGE,"E20.1.0"),sQuery(id+"F15.wireOp",EDGE,"E20.1.1")])]}),"instanceName":"1"});
            var Q2;
            Q2=makeQuery(id+"F22.opPattern","COPY",BODY,{"derivedFrom":makeQuery(id+"F17.opExtrude","SWEPT_BODY",BODY,{"disambiguationData":[OSD([sQuery(id+"F15.wireOp",EDGE,"E15"),sQuery(id+"F15.wireOp",EDGE,"E16"),sQuery(id+"F15.wireOp",EDGE,"E18"),sQuery(id+"F15.wireOp",EDGE,"E19.MirrorCS")])]}),"instanceName":"1"});
            var Q3;
            Q3=makeQuery(id+"F22.opPattern","COPY",BODY,{"derivedFrom":makeQuery(id+"F17.opExtrude","SWEPT_BODY",BODY,{"disambiguationData":[OSD([sQuery(id+"F15.wireOp",EDGE,"E15"),sQuery(id+"F15.wireOp",EDGE,"E16"),sQuery(id+"F15.wireOp",EDGE,"E20.3.1"),sQuery(id+"F15.wireOp",EDGE,"E20.3.0")])]}),"instanceName":"1"});
            var Q4;
            Q4=makeQuery(id+"F22.opPattern","COPY",BODY,{"derivedFrom":makeQuery(id+"F16.opExtrude","SWEPT_BODY",BODY,{"disambiguationData":[OSD([sQuery(id+"F15.wireOp",EDGE,"E15"),sQuery(id+"F15.wireOp",EDGE,"E23"),sQuery(id+"F15.wireOp",EDGE,"E24"),sQuery(id+"F15.wireOp",EDGE,"E25"),sQuery(id+"F15.wireOp",EDGE,"E26"),sQuery(id+"F15.wireOp",EDGE,"E27.filletArc"),sQuery(id+"F15.wireOp",EDGE,"E28.MirrorCS"),sQuery(id+"F15.wireOp",EDGE,"E30.MirrorCS"),sQuery(id+"F15.wireOp",EDGE,"E31.MirrorCS"),sQuery(id+"F15.wireOp",EDGE,"E32.MirrorCS"),sQuery(id+"F15.wireOp",EDGE,"E33.trimOffspring"),sQuery(id+"F15.wireOp",EDGE,"E35"),sQuery(id+"F15.wireOp",EDGE,"E41"),sQuery(id+"F15.wireOp",EDGE,"E42"),sQuery(id+"F15.wireOp",EDGE,"E44"),sQuery(id+"F15.wireOp",EDGE,"E45"),sQuery(id+"F15.wireOp",EDGE,"E46.trimOffspring"),sQuery(id+"F15.wireOp",EDGE,"E48"),sQuery(id+"F15.wireOp",EDGE,"E49"),sQuery(id+"F15.wireOp",EDGE,"E50"),sQuery(id+"F15.wireOp",EDGE,"E51.trimOffspring"),sQuery(id+"F15.wireOp",EDGE,"E52.trimOffspring"),sQuery(id+"F15.wireOp",EDGE,"E53.trimOffspring"),sQuery(id+"F15.wireOp",EDGE,"E54.filletArc"),sQuery(id+"F15.wireOp",EDGE,"E55.filletArc"),sQuery(id+"F15.wireOp",EDGE,"E56.filletArc"),sQuery(id+"F15.wireOp",EDGE,"E57.filletArc"),sQuery(id+"F15.wireOp",EDGE,"E58.filletArc"),sQuery(id+"F15.wireOp",EDGE,"E59.filletArc"),sQuery(id+"F15.wireOp",EDGE,"E61.MirrorCS"),sQuery(id+"F15.wireOp",EDGE,"E62.MirrorCS"),sQuery(id+"F15.wireOp",EDGE,"E63.MirrorCS"),sQuery(id+"F15.wireOp",EDGE,"E65.MirrorCS"),sQuery(id+"F15.wireOp",EDGE,"E66.MirrorCS"),sQuery(id+"F15.wireOp",EDGE,"E67.MirrorCS"),sQuery(id+"F15.wireOp",EDGE,"E68.MirrorCS"),sQuery(id+"F15.wireOp",EDGE,"E69.MirrorCS"),sQuery(id+"F15.wireOp",EDGE,"E70.MirrorCS"),sQuery(id+"F15.wireOp",EDGE,"E75.MirrorCS"),sQuery(id+"F15.wireOp",EDGE,"E76.MirrorCS"),sQuery(id+"F15.wireOp",EDGE,"E79.MirrorCS"),sQuery(id+"F15.wireOp",EDGE,"E80.MirrorCS"),sQuery(id+"F15.wireOp",EDGE,"E84.MirrorCS"),sQuery(id+"F15.wireOp",EDGE,"E85.MirrorCS"),sQuery(id+"F15.wireOp",EDGE,"E86.MirrorCS")])]}),"instanceName":"1"});
            var Q5;
            Q5=makeQuery(id+"F17.opExtrude","SWEPT_BODY",BODY,{"disambiguationData":[OSD([sQuery(id+"F15.wireOp",EDGE,"E15"),sQuery(id+"F15.wireOp",EDGE,"E16"),sQuery(id+"F15.wireOp",EDGE,"E20.2.0"),sQuery(id+"F15.wireOp",EDGE,"E20.2.1")])]});
            var Q6;
            Q6=makeQuery(id+"F17.opExtrude","SWEPT_BODY",BODY,{"disambiguationData":[OSD([sQuery(id+"F15.wireOp",EDGE,"E15"),sQuery(id+"F15.wireOp",EDGE,"E16"),sQuery(id+"F15.wireOp",EDGE,"E20.1.0"),sQuery(id+"F15.wireOp",EDGE,"E20.1.1")])]});
            var Q7;
            Q7=makeQuery(id+"F17.opExtrude","SWEPT_BODY",BODY,{"disambiguationData":[OSD([sQuery(id+"F15.wireOp",EDGE,"E15"),sQuery(id+"F15.wireOp",EDGE,"E16"),sQuery(id+"F15.wireOp",EDGE,"E18"),sQuery(id+"F15.wireOp",EDGE,"E19.MirrorCS")])]});
            var Q8;
            Q8=makeQuery(id+"F17.opExtrude","SWEPT_BODY",BODY,{"disambiguationData":[OSD([sQuery(id+"F15.wireOp",EDGE,"E15"),sQuery(id+"F15.wireOp",EDGE,"E16"),sQuery(id+"F15.wireOp",EDGE,"E20.3.1"),sQuery(id+"F15.wireOp",EDGE,"E20.3.0")])]});
            var Q9;
            Q9=makeQuery(id+"F16.opExtrude","SWEPT_BODY",BODY,{"disambiguationData":[OSD([sQuery(id+"F15.wireOp",EDGE,"E15"),sQuery(id+"F15.wireOp",EDGE,"E23"),sQuery(id+"F15.wireOp",EDGE,"E24"),sQuery(id+"F15.wireOp",EDGE,"E25"),sQuery(id+"F15.wireOp",EDGE,"E26"),sQuery(id+"F15.wireOp",EDGE,"E27.filletArc"),sQuery(id+"F15.wireOp",EDGE,"E28.MirrorCS"),sQuery(id+"F15.wireOp",EDGE,"E30.MirrorCS"),sQuery(id+"F15.wireOp",EDGE,"E31.MirrorCS"),sQuery(id+"F15.wireOp",EDGE,"E32.MirrorCS"),sQuery(id+"F15.wireOp",EDGE,"E33.trimOffspring"),sQuery(id+"F15.wireOp",EDGE,"E35"),sQuery(id+"F15.wireOp",EDGE,"E41"),sQuery(id+"F15.wireOp",EDGE,"E42"),sQuery(id+"F15.wireOp",EDGE,"E44"),sQuery(id+"F15.wireOp",EDGE,"E45"),sQuery(id+"F15.wireOp",EDGE,"E46.trimOffspring"),sQuery(id+"F15.wireOp",EDGE,"E48"),sQuery(id+"F15.wireOp",EDGE,"E49"),sQuery(id+"F15.wireOp",EDGE,"E50"),sQuery(id+"F15.wireOp",EDGE,"E51.trimOffspring"),sQuery(id+"F15.wireOp",EDGE,"E52.trimOffspring"),sQuery(id+"F15.wireOp",EDGE,"E53.trimOffspring"),sQuery(id+"F15.wireOp",EDGE,"E54.filletArc"),sQuery(id+"F15.wireOp",EDGE,"E55.filletArc"),sQuery(id+"F15.wireOp",EDGE,"E56.filletArc"),sQuery(id+"F15.wireOp",EDGE,"E57.filletArc"),sQuery(id+"F15.wireOp",EDGE,"E58.filletArc"),sQuery(id+"F15.wireOp",EDGE,"E59.filletArc"),sQuery(id+"F15.wireOp",EDGE,"E61.MirrorCS"),sQuery(id+"F15.wireOp",EDGE,"E62.MirrorCS"),sQuery(id+"F15.wireOp",EDGE,"E63.MirrorCS"),sQuery(id+"F15.wireOp",EDGE,"E65.MirrorCS"),sQuery(id+"F15.wireOp",EDGE,"E66.MirrorCS"),sQuery(id+"F15.wireOp",EDGE,"E67.MirrorCS"),sQuery(id+"F15.wireOp",EDGE,"E68.MirrorCS"),sQuery(id+"F15.wireOp",EDGE,"E69.MirrorCS"),sQuery(id+"F15.wireOp",EDGE,"E70.MirrorCS"),sQuery(id+"F15.wireOp",EDGE,"E75.MirrorCS"),sQuery(id+"F15.wireOp",EDGE,"E76.MirrorCS"),sQuery(id+"F15.wireOp",EDGE,"E79.MirrorCS"),sQuery(id+"F15.wireOp",EDGE,"E80.MirrorCS"),sQuery(id+"F15.wireOp",EDGE,"E84.MirrorCS"),sQuery(id+"F15.wireOp",EDGE,"E85.MirrorCS"),sQuery(id+"F15.wireOp",EDGE,"E86.MirrorCS")])]});
            var Q10;
            Q10=sQuery(id+"F2.wireOp",EDGE,"E5");
            circularPattern(context, id + "F23", {"entities" : qUnion([Q0, Q1, Q2, Q3, Q4, Q5, Q6, Q7, Q8, Q9]), "axis" : qUnion([Q10]), "angle" : 360 * degree, "instanceCount" : 4, "equalSpace" : true});
        }
    });
